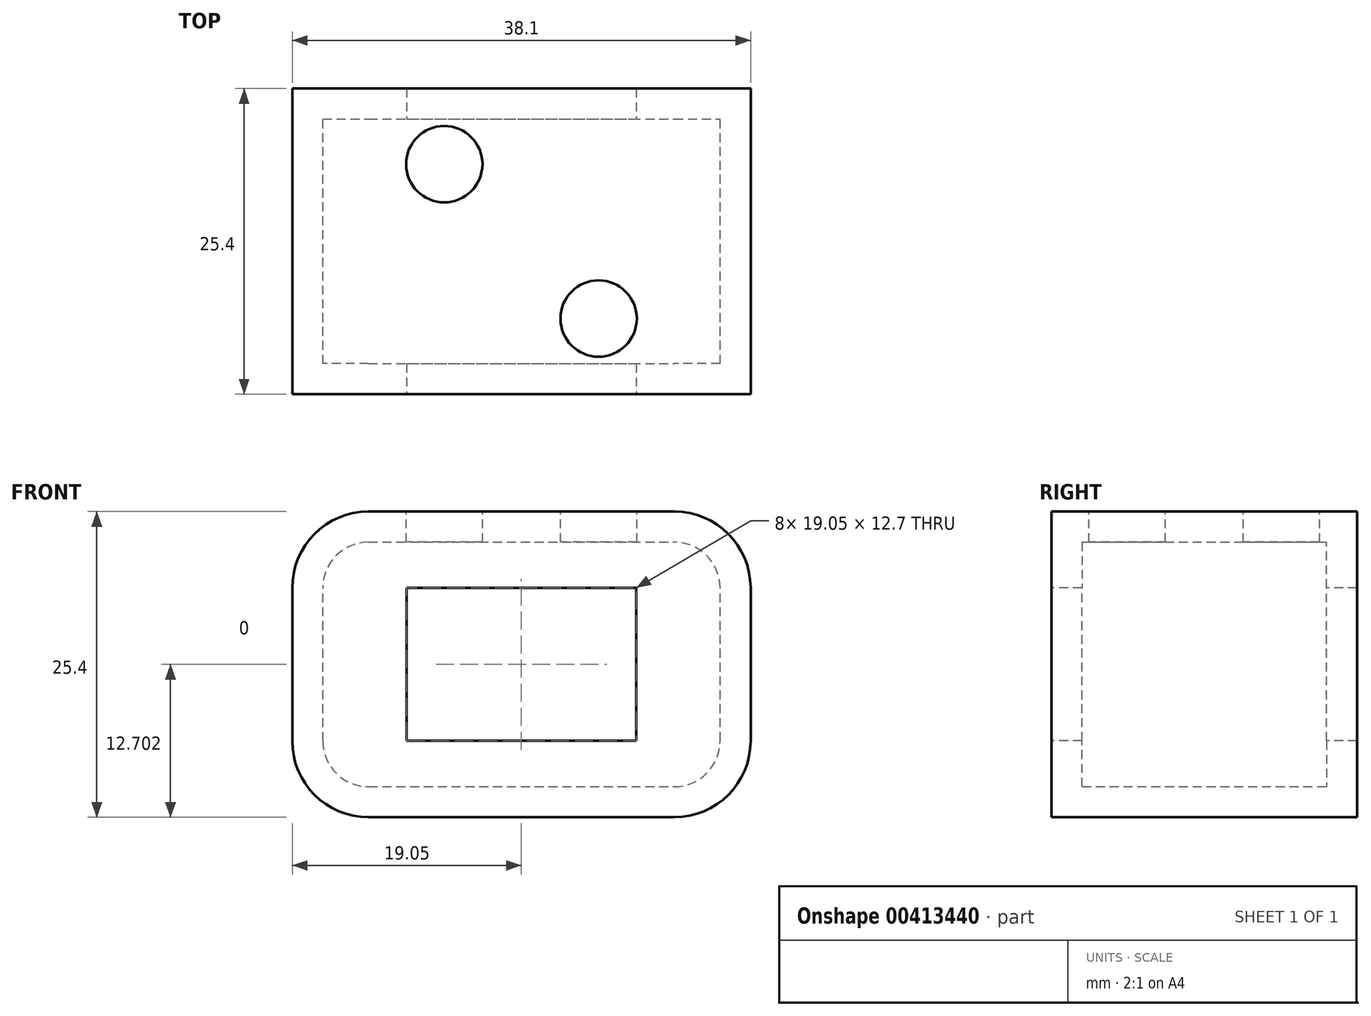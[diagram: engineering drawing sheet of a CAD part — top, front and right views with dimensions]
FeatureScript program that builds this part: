
annotation { "Feature Type Name" : "Feature", "Feature Type Description" : "" }
export const myFeature = defineFeature(function(context is Context, id is Id, definition is map)
    precondition{}
    {
        {
            var Q0;
            Q0=qCreatedBy(makeId("Front.planeOp"),FACE);
            var sketch = newSketch(context, id + "F0", { "sketchPlane" : qUnion([Q0])});
            skLineSegment(sketch, "E0.bottom", {"start": v(6.35, 1.03) * mm, "end": v(31.75, 1.03) * mm});
            skLineSegment(sketch, "E0.top", {"start": v(6.35, 26.43) * mm, "end": v(31.75, 26.43) * mm});
            skLineSegment(sketch, "E0.left", {"start": v(0, 7.38) * mm, "end": v(0, 20.08) * mm});
            skLineSegment(sketch, "E0.right", {"start": v(38.1, 7.38) * mm, "end": v(38.1, 20.08) * mm});
            skPoint(sketch, "E1.visualSharp", {"position": v(0, 26.43) * mm});
            skArc(sketch, "E1.filletArc", {"start": v(6.35, 26.43) * mm, "mid": v(1.86, 24.57) * mm, "end": v(0, 20.08) * mm});
            skPoint(sketch, "E2.visualSharp", {"position": v(0, 1.03) * mm});
            skArc(sketch, "E2.filletArc", {"start": v(0, 7.38) * mm, "mid": v(1.86, 2.9) * mm, "end": v(6.35, 1.03) * mm});
            skPoint(sketch, "E3.visualSharp", {"position": v(38.1, 1.03) * mm});
            skArc(sketch, "E3.filletArc", {"start": v(31.75, 1.03) * mm, "mid": v(36.24, 2.9) * mm, "end": v(38.1, 7.38) * mm});
            skPoint(sketch, "E4.visualSharp", {"position": v(38.1, 26.43) * mm});
            skArc(sketch, "E4.filletArc", {"start": v(38.1, 20.08) * mm, "mid": v(36.24, 24.57) * mm, "end": v(31.75, 26.43) * mm});
            skSolve(sketch);
        }
        {
            var Q0;
            Q0 = qSketchRegion(id + "F0", true);
            extrude(context, id + "F1", {"entities" : qUnion([Q0]), "depth" : 25.4 * mm});
        }
        {
            var Q0;
            Q0=makeQuery(id+"F1.opExtrude","CAP_FACE",FACE,{"disambiguationData":[OSD([sQuery(id+"F0.wireOp",EDGE,"E0.bottom"),sQuery(id+"F0.wireOp",EDGE,"E0.top"),sQuery(id+"F0.wireOp",EDGE,"E0.left"),sQuery(id+"F0.wireOp",EDGE,"E0.right"),sQuery(id+"F0.wireOp",EDGE,"E1.filletArc"),sQuery(id+"F0.wireOp",EDGE,"E2.filletArc"),sQuery(id+"F0.wireOp",EDGE,"E3.filletArc"),sQuery(id+"F0.wireOp",EDGE,"E4.filletArc")])],"isStart":false});
            var sketch = newSketch(context, id + "F2", { "sketchPlane" : qUnion([Q0])});
            skLineSegment(sketch, "E5.bottom", {"start": v(9.52, 7.38) * mm, "end": v(28.58, 7.38) * mm});
            skLineSegment(sketch, "E5.top", {"start": v(9.52, 20.08) * mm, "end": v(28.58, 20.08) * mm});
            skLineSegment(sketch, "E5.left", {"start": v(9.53, 7.38) * mm, "end": v(9.52, 20.08) * mm});
            skLineSegment(sketch, "E5.right", {"start": v(28.57, 7.38) * mm, "end": v(28.57, 20.08) * mm});
            skLineSegment(sketch, "E6", {"start": v(19.05, 20.08) * mm, "end": v(19.05, 7.38) * mm, "construction": true});
            skLineSegment(sketch, "E7", {"start": v(9.52, 13.73) * mm, "end": v(28.58, 13.73) * mm, "construction": true});
            skSolve(sketch);
        }
        {
            var Q0;
            Q0 = qSketchRegion(id + "F2", true);
            extrude(context, id + "F3", {"entities" : qUnion([Q0]), "operationType" : NewBodyOperationType.REMOVE, "endBound" : BoundingType.THROUGH_ALL, "oppositeDirection" : true, "depth" : 25.4 * mm});
        }
        {
            var Q0;
            Q0=makeQuery(id+"F3.boolean.opBoolean","COPY",FACE,{"derivedFrom":makeQuery(id+"F3.opExtrude","SWEPT_FACE",FACE,{"disambiguationData":[OSD([sQuery(id+"F2.wireOp",EDGE,"E5.left")])]})});
            var Q1;
            Q1=makeQuery(id+"F3.boolean.opBoolean","COPY",FACE,{"derivedFrom":makeQuery(id+"F3.opExtrude","SWEPT_FACE",FACE,{"disambiguationData":[OSD([sQuery(id+"F2.wireOp",EDGE,"E5.top")])]})});
            var Q2;
            Q2=makeQuery(id+"F3.boolean.opBoolean","COPY",FACE,{"derivedFrom":makeQuery(id+"F3.opExtrude","SWEPT_FACE",FACE,{"disambiguationData":[OSD([sQuery(id+"F2.wireOp",EDGE,"E5.bottom")])]})});
            var Q3;
            Q3=makeQuery(id+"F3.boolean.opBoolean","COPY",FACE,{"derivedFrom":makeQuery(id+"F3.opExtrude","SWEPT_FACE",FACE,{"disambiguationData":[OSD([sQuery(id+"F2.wireOp",EDGE,"E5.right")])]})});
            shell(context, id + "F4", {"entities" : qUnion([Q0, Q1, Q2, Q3]), "thickness" : 2.54 * mm});
        }
        {
            var Q0;
            Q0=makeQuery(id+"F1.opExtrude","SWEPT_FACE",FACE,{"disambiguationData":[OSD([sQuery(id+"F0.wireOp",EDGE,"E0.top")])]});
            var sketch = newSketch(context, id + "F5", { "sketchPlane" : qUnion([Q0])});
            skPoint(sketch, "E8", {"position": v(12.64, -6.29) * mm});
            skPoint(sketch, "E9", {"position": v(25.46, -19.11) * mm});
            skLineSegment(sketch, "E10", {"start": v(6.35, 0) * mm, "end": v(31.75, -25.4) * mm});
            skSolve(sketch);
        }
        {
            var Q0;
            Q0=sQuery(id+"F5.wireOp",VERTEX,"E8");
            var Q1;
            Q1=sQuery(id+"F5.wireOp",VERTEX,"E9");
            var Q2;
            Q2=makeQuery(id+"F1.opExtrude","SWEPT_BODY",BODY,{"disambiguationData":[OSD([sQuery(id+"F0.wireOp",EDGE,"E0.bottom"),sQuery(id+"F0.wireOp",EDGE,"E0.top"),sQuery(id+"F0.wireOp",EDGE,"E0.left"),sQuery(id+"F0.wireOp",EDGE,"E0.right"),sQuery(id+"F0.wireOp",EDGE,"E1.filletArc"),sQuery(id+"F0.wireOp",EDGE,"E2.filletArc"),sQuery(id+"F0.wireOp",EDGE,"E3.filletArc"),sQuery(id+"F0.wireOp",EDGE,"E4.filletArc")])]});
            hole(context, id + "F6", {"style" : HoleStyle.SIMPLE, "endStyle" : HoleEndStyle.BLIND, "holeDiameter" : 6.35 * mm, "holeDepth" : 12.7 * mm, "isTappedThrough" : true, "tappedDepth" : 12.7 * mm, "tapClearance" : 3, "locations" : qUnion([Q0, Q1]), "scope" : qUnion([Q2])});
        }
    });
